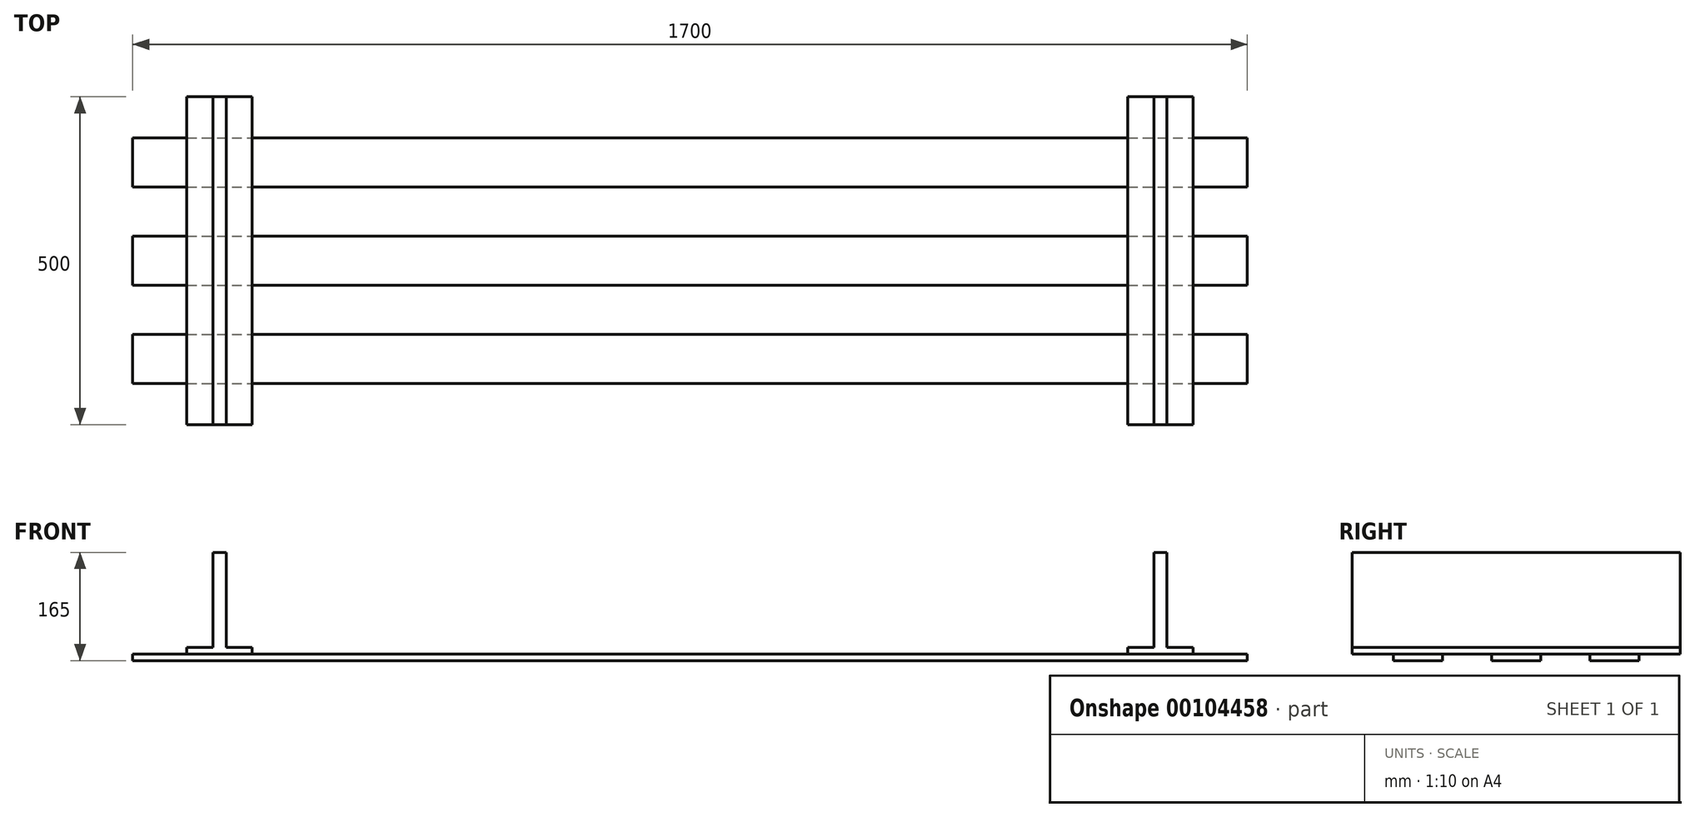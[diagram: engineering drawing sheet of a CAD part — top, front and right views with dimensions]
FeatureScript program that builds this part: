
annotation { "Feature Type Name" : "Feature", "Feature Type Description" : "" }
export const myFeature = defineFeature(function(context is Context, id is Id, definition is map)
    precondition{}
    {
        {
            var Q0;
            Q0=qCreatedBy(makeId("Front.planeOp"),FACE);
            var sketch = newSketch(context, id + "F0", { "sketchPlane" : qUnion([Q0])});
            skLineSegment(sketch, "E0", {"start": v(0, 0) * mm, "end": v(-717.5, 0) * mm, "construction": true});
            skLineSegment(sketch, "E1.bottom", {"start": v(-767.5, 5) * mm, "end": v(-667.5, 5) * mm});
            skLineSegment(sketch, "E1.top", {"start": v(-767.5, -5) * mm, "end": v(-667.5, -5) * mm});
            skLineSegment(sketch, "E1.left", {"start": v(-767.5, 5) * mm, "end": v(-767.5, -5) * mm});
            skLineSegment(sketch, "E1.right", {"start": v(-667.5, 5) * mm, "end": v(-667.5, -5) * mm});
            skPoint(sketch, "E1.middle", {"position": v(-717.5, 0) * mm});
            skLineSegment(sketch, "E2", {"start": v(-717.5, 0) * mm, "end": v(-717.5, 150) * mm, "construction": true});
            skLineSegment(sketch, "E3", {"start": v(-717.5, 150) * mm, "end": v(-727.5, 150) * mm});
            skLineSegment(sketch, "E4", {"start": v(-727.5, 150) * mm, "end": v(-727.5, 5) * mm});
            skLineSegment(sketch, "E5.MirrorCS", {"start": v(-707.5, 150) * mm, "end": v(-707.5, 5) * mm});
            skLineSegment(sketch, "E6", {"start": v(-717.5, 150) * mm, "end": v(-707.5, 150) * mm});
            skLineSegment(sketch, "E7", {"start": v(0, 0) * mm, "end": v(0, 150) * mm, "construction": true});
            skLineSegment(sketch, "E8.MirrorCS", {"start": v(667.5, 5) * mm, "end": v(667.5, -5) * mm});
            skLineSegment(sketch, "E9.MirrorCS", {"start": v(717.5, 150) * mm, "end": v(707.5, 150) * mm});
            skLineSegment(sketch, "E10.MirrorCS", {"start": v(767.5, 5) * mm, "end": v(767.5, -5) * mm});
            skLineSegment(sketch, "E11.MirrorCS", {"start": v(717.5, 150) * mm, "end": v(727.5, 150) * mm});
            skLineSegment(sketch, "E12.MirrorCS", {"start": v(767.5, 5) * mm, "end": v(667.5, 5) * mm});
            skLineSegment(sketch, "E13.MirrorCS", {"start": v(767.5, -5) * mm, "end": v(667.5, -5) * mm});
            skLineSegment(sketch, "E14.MirrorCS", {"start": v(717.5, 0) * mm, "end": v(717.5, 150) * mm, "construction": true});
            skLineSegment(sketch, "E15.MirrorCS", {"start": v(707.5, 150) * mm, "end": v(707.5, 5) * mm});
            skPoint(sketch, "E16.MirrorP", {"position": v(717.5, 0) * mm});
            skLineSegment(sketch, "E17.MirrorCS", {"start": v(727.5, 150) * mm, "end": v(727.5, 5) * mm});
            skSolve(sketch);
        }
        {
            var Q0;
            Q0 = qSketchRegion(id + "F0", true);
            extrude(context, id + "F1", {"entities" : qUnion([Q0]), "depth" : 500 * mm, "symmetric" : true});
        }
        {
            var Q0;
            Q0=makeQuery(id+"F1.opExtrude","SWEPT_FACE",FACE,{"disambiguationData":[OSD([sQuery(id+"F0.wireOp",EDGE,"E1.top")])]});
            var sketch = newSketch(context, id + "F2", { "sketchPlane" : qUnion([Q0])});
            skLineSegment(sketch, "E18.bottom", {"start": v(-850, 37.5) * mm, "end": v(850, 37.5) * mm});
            skLineSegment(sketch, "E18.top", {"start": v(-850, -37.5) * mm, "end": v(850, -37.5) * mm});
            skLineSegment(sketch, "E18.left", {"start": v(-850, 37.5) * mm, "end": v(-850, -37.5) * mm});
            skLineSegment(sketch, "E18.right", {"start": v(850, 37.5) * mm, "end": v(850, -37.5) * mm});
            skPoint(sketch, "E18.middle", {"position": v(0, 0) * mm});
            skLineSegment(sketch, "E19.0.1.0", {"start": v(850, 187.5) * mm, "end": v(850, 112.5) * mm});
            skLineSegment(sketch, "E19.0.1.1", {"start": v(-850, 187.5) * mm, "end": v(-850, 112.5) * mm});
            skLineSegment(sketch, "E19.0.1.2", {"start": v(-850, 112.5) * mm, "end": v(850, 112.5) * mm});
            skLineSegment(sketch, "E19.0.1.3", {"start": v(-850, 187.5) * mm, "end": v(850, 187.5) * mm});
            skPoint(sketch, "E19.0.1.4", {"position": v(0, 150) * mm});
            skLineSegment(sketch, "E19.direction1", {"start": v(-850, -37.5) * mm, "end": v(-825, -37.5) * mm, "construction": true});
            skLineSegment(sketch, "E19.direction2", {"start": v(-850, -37.5) * mm, "end": v(-850, 112.5) * mm, "construction": true});
            skPoint(sketch, "E20.0.1.0", {"position": v(0, -150) * mm});
            skLineSegment(sketch, "E20.0.1.1", {"start": v(-850, -112.5) * mm, "end": v(850, -112.5) * mm});
            skLineSegment(sketch, "E20.0.1.2", {"start": v(-850, -187.5) * mm, "end": v(850, -187.5) * mm});
            skLineSegment(sketch, "E20.0.1.3", {"start": v(-850, -112.5) * mm, "end": v(-850, -187.5) * mm});
            skLineSegment(sketch, "E20.0.1.4", {"start": v(850, -112.5) * mm, "end": v(850, -187.5) * mm});
            skLineSegment(sketch, "E20.0.1.5", {"start": v(-850, -187.5) * mm, "end": v(-825, -187.5) * mm, "construction": true});
            skLineSegment(sketch, "E20.direction2", {"start": v(-850, -37.5) * mm, "end": v(-850, -187.5) * mm, "construction": true});
            skSolve(sketch);
        }
        {
            var Q0;
            Q0 = qSketchRegion(id + "F2", true);
            extrude(context, id + "F3", {"entities" : qUnion([Q0]), "depth" : 10 * mm});
        }
    });
